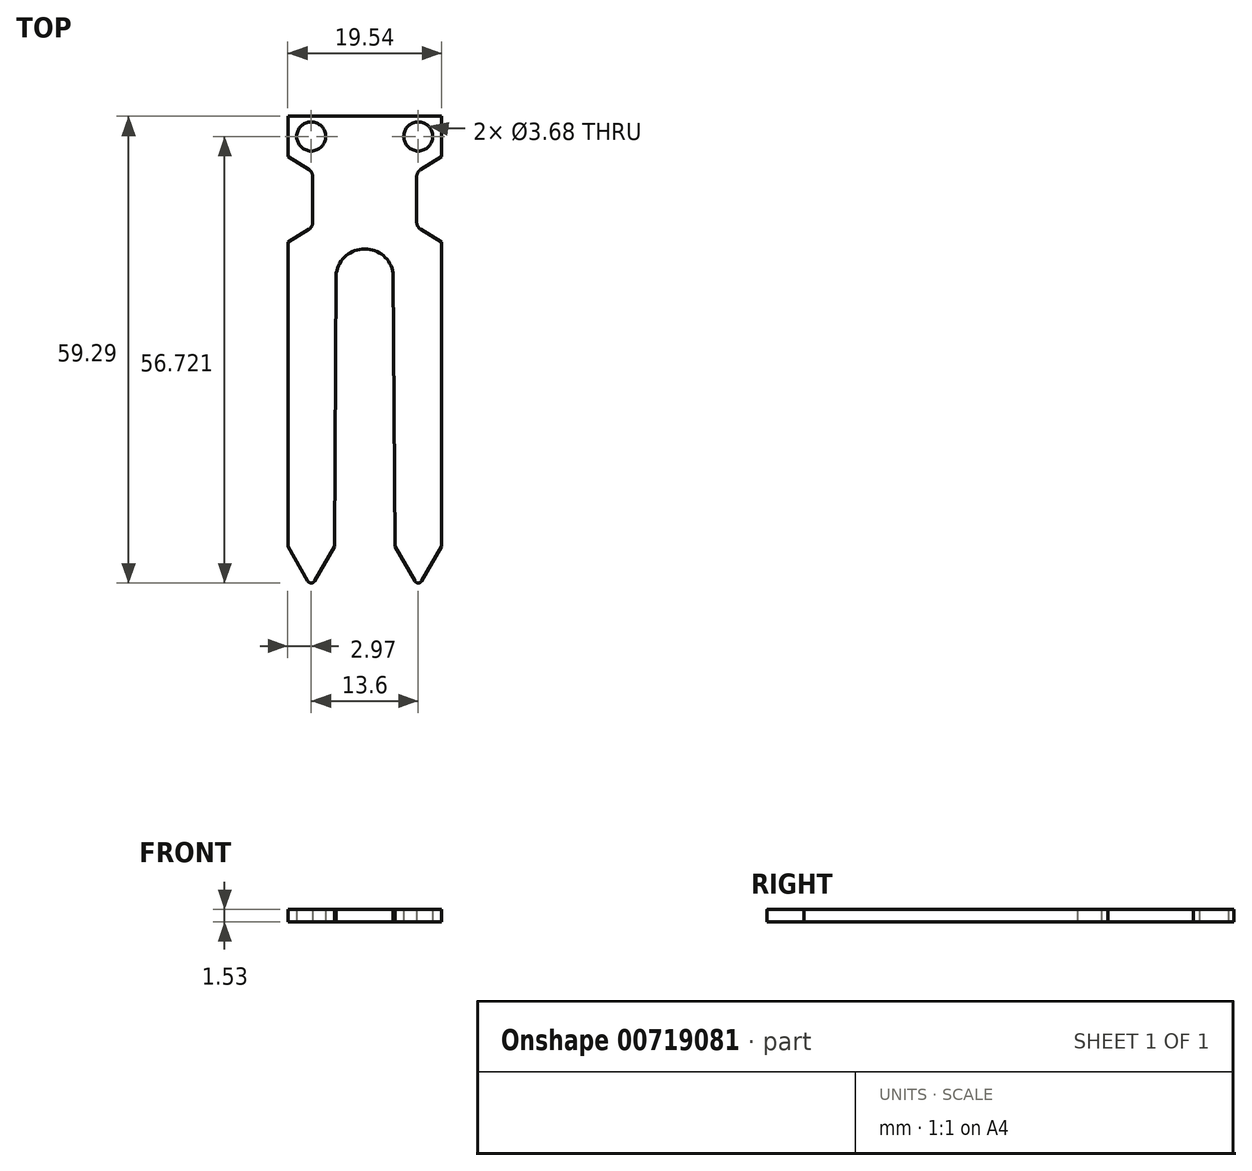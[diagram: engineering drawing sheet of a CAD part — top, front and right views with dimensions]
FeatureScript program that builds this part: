
annotation { "Feature Type Name" : "Feature", "Feature Type Description" : "" }
export const myFeature = defineFeature(function(context is Context, id is Id, definition is map)
    precondition{}
    {
        {
            var Q0;
            Q0=qCreatedBy(makeId("Top.planeOp"),FACE);
            var sketch = newSketch(context, id + "F0", { "sketchPlane" : qUnion([Q0])});
            skLineSegment(sketch, "E0", {"start": v(-9.76, 25.18) * mm, "end": v(-9.76, 23.54) * mm});
            skLineSegment(sketch, "E1", {"start": v(-3.83, -25.96) * mm, "end": v(-3.61, 8.77) * mm});
            skLineSegment(sketch, "E2", {"start": v(-9.76, -25.96) * mm, "end": v(-3.83, -25.96) * mm});
            skLineSegment(sketch, "E3", {"start": v(-9.76, -25.96) * mm, "end": v(-6.8, -31.1) * mm});
            skLineSegment(sketch, "E4", {"start": v(-6.8, -31.1) * mm, "end": v(-3.83, -25.96) * mm});
            skLineSegment(sketch, "E5.MirrorCS", {"start": v(9.76, 25.18) * mm, "end": v(9.76, 23.54) * mm});
            skLineSegment(sketch, "E6.MirrorCS", {"start": v(3.83, -25.96) * mm, "end": v(3.61, 8.77) * mm});
            skLineSegment(sketch, "E7.MirrorCS", {"start": v(9.76, -25.96) * mm, "end": v(3.83, -25.96) * mm});
            skLineSegment(sketch, "E8.MirrorCS", {"start": v(9.76, -25.96) * mm, "end": v(6.8, -31.1) * mm});
            skLineSegment(sketch, "E9.MirrorCS", {"start": v(6.8, -31.1) * mm, "end": v(3.83, -25.96) * mm});
            skLineSegment(sketch, "E10", {"start": v(-9.76, -25.96) * mm, "end": v(-9.76, 12.7) * mm});
            skLineSegment(sketch, "E11", {"start": v(9.77, 28.7) * mm, "end": v(9.76, 23.54) * mm});
            skCircle(sketch, "E12", {"center": v(-6.8, 26.12) * mm, "radius": 1.84 * mm});
            skPoint(sketch, "E13", {"position": v(-9.76, 23.54) * mm});
            skPoint(sketch, "E14", {"position": v(-9.76, 12.7) * mm});
            skPoint(sketch, "E15.MirrorP", {"position": v(9.76, 23.54) * mm});
            skPoint(sketch, "E16.MirrorP", {"position": v(9.76, 12.7) * mm});
            skCircle(sketch, "E17.MirrorC", {"center": v(6.8, 26.12) * mm, "radius": 1.84 * mm});
            skPoint(sketch, "E18", {"position": v(-6.61, 21.61) * mm});
            skPoint(sketch, "E19", {"position": v(-6.61, 14.62) * mm});
            skLineSegment(sketch, "E20.trimOffspring", {"start": v(-9.76, 12.7) * mm, "end": v(-9.76, -25.96) * mm});
            skLineSegment(sketch, "E21.trimOffspring", {"start": v(-9.76, 23.54) * mm, "end": v(-9.77, 28.7) * mm});
            skLineSegment(sketch, "E22", {"start": v(-9.76, 23.54) * mm, "end": v(-6.61, 21.61) * mm});
            skLineSegment(sketch, "E23", {"start": v(-6.61, 14.62) * mm, "end": v(-9.76, 12.7) * mm});
            skLineSegment(sketch, "E24", {"start": v(-6.61, 14.62) * mm, "end": v(-6.61, 21.61) * mm});
            skLineSegment(sketch, "E25.MirrorCS", {"start": v(9.76, 23.54) * mm, "end": v(6.61, 21.61) * mm});
            skLineSegment(sketch, "E26.MirrorCS", {"start": v(6.61, 14.62) * mm, "end": v(6.61, 21.61) * mm});
            skLineSegment(sketch, "E27.MirrorCS", {"start": v(6.61, 14.62) * mm, "end": v(9.76, 12.7) * mm});
            skLineSegment(sketch, "E28.trimOffspring", {"start": v(9.76, 12.7) * mm, "end": v(9.76, -25.96) * mm});
            skArc(sketch, "E29", {"start": v(3.61, 8.77) * mm, "mid": v(-0.57, 11.8) * mm, "end": v(-3.62, 7.63) * mm});
            skLineSegment(sketch, "E30", {"start": v(-9.77, 28.7) * mm, "end": v(9.76, 28.7) * mm});
            skPoint(sketch, "E31", {"position": v(-6.8, -25.96) * mm});
            skPoint(sketch, "E32", {"position": v(6.8, -25.96) * mm});
            skSolve(sketch);
        }
        {
            var Q0;
            Q0 = qSketchRegion(id + "F0", true);
            extrude(context, id + "F1", {"entities" : qUnion([Q0]), "depth" : 1.53 * mm, "offsetDistance" : 25 * mm});
        }
        {
            var Q0;
            Q0=makeQuery(id+"F1.opExtrude","SWEPT_EDGE",EDGE,{"disambiguationData":[OSD([sQuery(id+"F0.wireOp",EDGE,"E25.MirrorCS"),sQuery(id+"F0.wireOp",EDGE,"E26.MirrorCS")])]});
            var Q1;
            Q1=makeQuery(id+"F1.opExtrude","SWEPT_EDGE",EDGE,{"disambiguationData":[OSD([sQuery(id+"F0.wireOp",EDGE,"E26.MirrorCS"),sQuery(id+"F0.wireOp",EDGE,"E27.MirrorCS")])]});
            var Q2;
            Q2=makeQuery(id+"F1.opExtrude","SWEPT_EDGE",EDGE,{"disambiguationData":[OSD([sQuery(id+"F0.wireOp",EDGE,"E22"),sQuery(id+"F0.wireOp",EDGE,"E24")])]});
            var Q3;
            Q3=makeQuery(id+"F1.opExtrude","SWEPT_EDGE",EDGE,{"disambiguationData":[OSD([sQuery(id+"F0.wireOp",EDGE,"E23"),sQuery(id+"F0.wireOp",EDGE,"E24")])]});
            fillet(context, id + "F2", {"entities" : qUnion([Q0, Q1, Q2, Q3]), "radius" : 1 * mm, "tangentPropagation" : true, "allowEdgeOverflow" : false});
        }
        {
            var Q0;
            Q0=makeQuery(id+"F1.opExtrude","SWEPT_EDGE",EDGE,{"disambiguationData":[OSD([sQuery(id+"F0.wireOp",EDGE,"E3"),sQuery(id+"F0.wireOp",EDGE,"E4")])]});
            var Q1;
            Q1=makeQuery(id+"F1.opExtrude","SWEPT_EDGE",EDGE,{"disambiguationData":[OSD([sQuery(id+"F0.wireOp",EDGE,"E8.MirrorCS"),sQuery(id+"F0.wireOp",EDGE,"E9.MirrorCS")])]});
            fillet(context, id + "F3", {"entities" : qUnion([Q0, Q1]), "radius" : 0.5 * mm, "tangentPropagation" : true, "allowEdgeOverflow" : false});
        }
    });
